# Revit family: AF5300A 56-62
name_source: partatom
category: HLS-Bauteile
revit_build: Autodesk Revit 2017 (Build: 20160720_1515(x64)
units: mm (PartAtom-declared; Revit-internal decimal feet)

## family parameters
Arbeitsebenenbasiert = Nein
Beim Laden mit Abzugskörper schneiden = Nein
Bemaßung runder Anschluss = Durchmesser verwenden
Gemeinsam genutzt = Nein
Immer vertikal = Ja
OmniClass-Nummer = 23.75.00.00
OmniClass-Titel = Climate Control (HVAC)
Raumberechnungspunkt = Nein
Teiletyp = Normal

## types (2) — shared parameters
Air Flow max = 17000.000 m³/h
Beschreibung = High efficiency air cooled
Casing color = White
Compressor = 2
Condensation = Air
Depth = 825 mm  [stored 2.70669 ft]
Gas = R410A
Gas pipe = 31.8 mm  [stored 0.104331 ft]
Height = 1635 mm  [stored 5.36417 ft]
Hersteller = Bosch
Installation = Outdoor installation
Liquid pipe = 19.1 mm  [stored 0.062664 ft]
Machine material = Galvanized Steel
Maximum Fuse Amps = 70 A
Net Weight = 344.00 kg
Power supply = 380-415V 3N~50Hz/60Hz
Series = VRF
Width = 1340 mm
clearance access behind = 1000 mm  [stored 3.28084 ft]
clearance access front = 1000 mm  [stored 3.28084 ft]
clearance access left = 1000 mm  [stored 3.28084 ft]
clearance access right = 1000 mm  [stored 3.28084 ft]

## per-type parameters (varying)
| type | Cooling Capacity | Cooling Power Input | Heating Capacity | Heating Power Input | Minimum Circuit Amps |
| AF5300A 56-3 | 56.000 kW | 16.000 kW | 56.000 kW | 13.800 kW | 46 A |
| AF5300A 62-3 | 61.500 kW | 20.200 kW | 61.500 kW | 17.600 kW | 48 A |

note: column(s) folded — value = type name in every type: Modell

note: [stored X ft] marks values corroborated as IEEE doubles in the binary element streams (Revit-internal decimal feet)

## geometry (parser evidence)
native form markers: Sweep x5
no freeform markers — native parametric forms only
